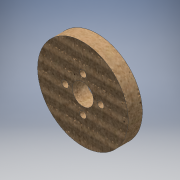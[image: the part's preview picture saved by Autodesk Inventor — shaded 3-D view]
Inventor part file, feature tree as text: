
AUTODESK INVENTOR PART (.ipt)
format: ipt  version: 2016 (Build 200138000, 138)  size: 154,112 bytes
history: native  units: mm
features: extrude x1, sketch x1
ambient origin geometry x8: Origin, YZ Plane, XZ Plane, XY Plane, X Axis, Y Axis, Z Axis, Center Point
bodies: Solid1 (feature_tree)
feature tree (2):
  extrude  "Extrusion1"  Depth=6.39mm TaperAngle=360.0deg
  sketch  "Sketch1"  dims[d0=40.592635mm d3=40.0mm d5=360.0deg d7=9.525mm d8=6.39mm d9=0.0mm]
